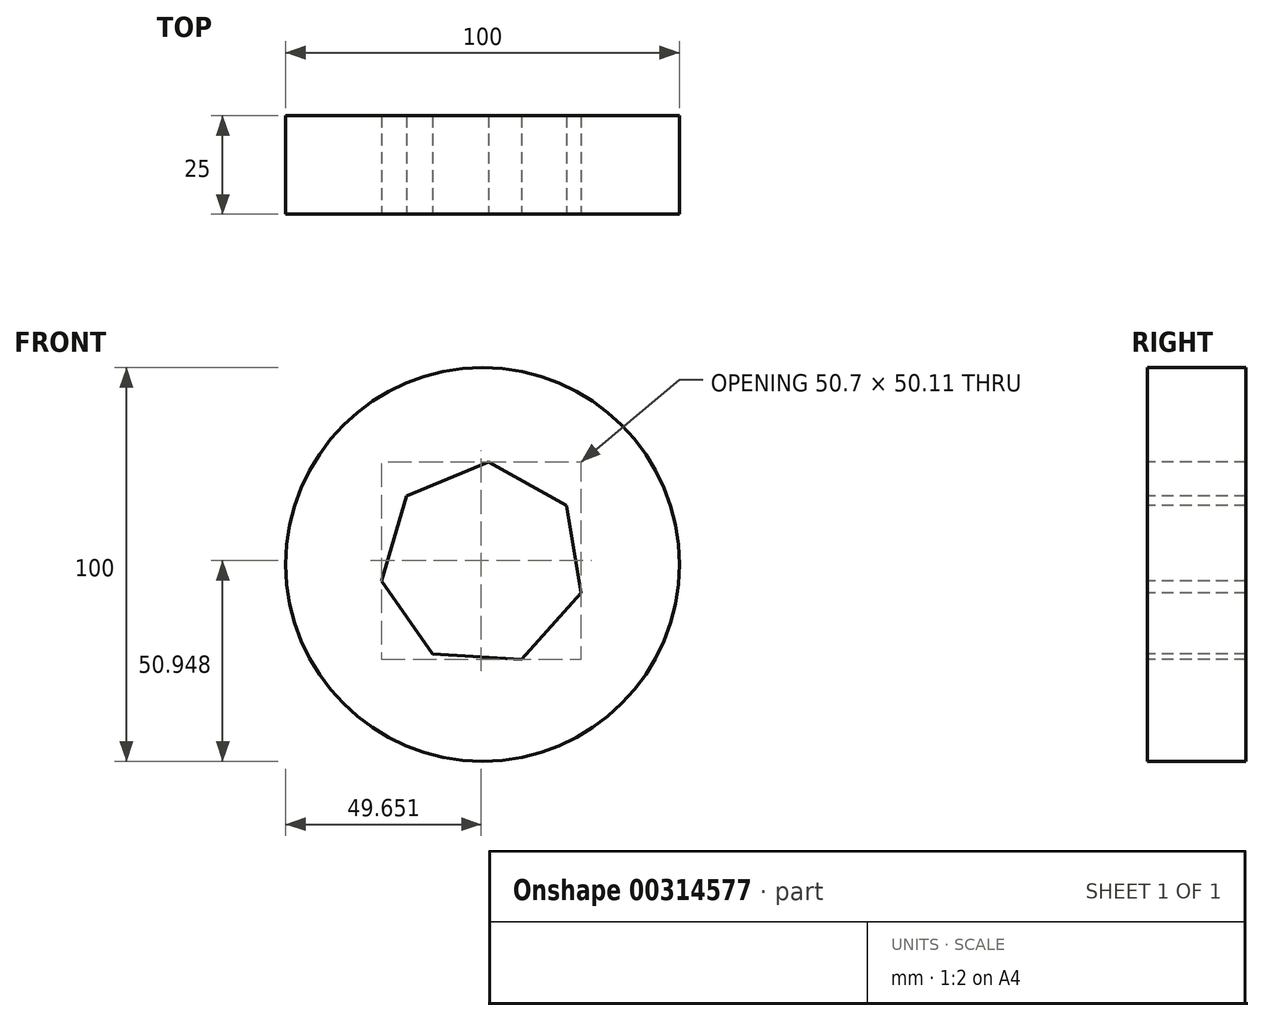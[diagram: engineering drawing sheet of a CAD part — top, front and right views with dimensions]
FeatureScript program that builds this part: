
annotation { "Feature Type Name" : "Feature", "Feature Type Description" : "" }
export const myFeature = defineFeature(function(context is Context, id is Id, definition is map)
    precondition{}
    {
        {
            var Q0;
            Q0=qCreatedBy(makeId("Front.planeOp"),FACE);
            var sketch = newSketch(context, id + "F0", { "sketchPlane" : qUnion([Q0])});
            skCircle(sketch, "E0", {"center": v(0, 0) * mm, "radius": 50 * mm});
            skSolve(sketch);
        }
        {
            var Q0;
            Q0 = qSketchRegion(id + "F0", true);
            extrude(context, id + "F1", {"entities" : qUnion([Q0]), "oppositeDirection" : true, "depth" : 25 * mm});
        }
        {
            var Q0;
            Q0=makeQuery(id+"F1.opExtrude","CAP_FACE",FACE,{"disambiguationData":[OSD([sQuery(id+"F0.wireOp",EDGE,"E0")])],"isStart":true});
            var sketch = newSketch(context, id + "F2", { "sketchPlane" : qUnion([Q0])});
            skCircle(sketch, "E1.cCircle", {"center": v(0, 0) * mm, "radius": 23.47 * mm, "construction": true});
            skLineSegment(sketch, "E1.0", {"start": v(-12.7, -22.75) * mm, "end": v(-25.7, -4.26) * mm});
            skLineSegment(sketch, "E1.1", {"start": v(-25.7, -4.26) * mm, "end": v(-19.35, 17.44) * mm});
            skLineSegment(sketch, "E1.2", {"start": v(-19.35, 17.44) * mm, "end": v(1.57, 26) * mm});
            skLineSegment(sketch, "E1.3", {"start": v(1.57, 26) * mm, "end": v(21.3, 14.99) * mm});
            skLineSegment(sketch, "E1.4", {"start": v(21.3, 14.99) * mm, "end": v(25, -7.31) * mm});
            skLineSegment(sketch, "E1.5", {"start": v(25, -7.31) * mm, "end": v(9.87, -24.1) * mm});
            skLineSegment(sketch, "E1.6", {"start": v(9.87, -24.1) * mm, "end": v(-12.7, -22.75) * mm});
            skPoint(sketch, "E1.0.midPoint", {"position": v(-19.2, -13.5) * mm});
            skSolve(sketch);
        }
        {
            var Q0;
            Q0=makeQuery(id+"F2.imprint","IMPRINT",FACE,{"disambiguationData":[TD([[makeQuery(id+"F2.imprint","IMPRINT",EDGE,{"derivedFrom":sQuery(id+"F2.wireOp",EDGE,"E1.0")}),-1.0]])]});
            extrude(context, id + "F3", {"entities" : qUnion([Q0]), "operationType" : NewBodyOperationType.REMOVE, "endBound" : BoundingType.THROUGH_ALL, "oppositeDirection" : true, "depth" : 25 * mm});
        }
    });
